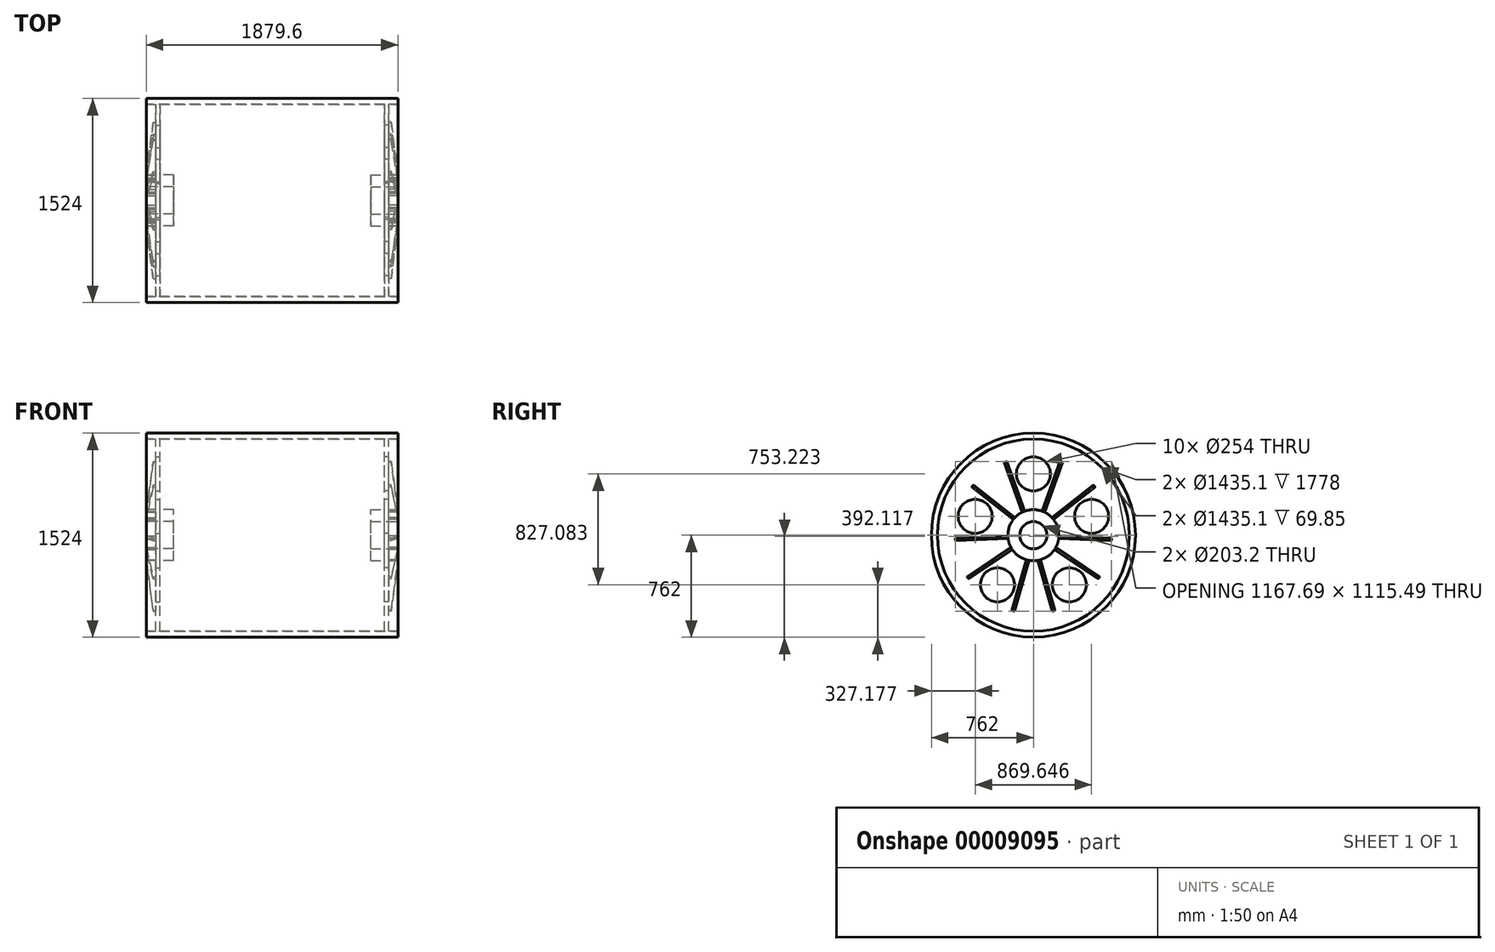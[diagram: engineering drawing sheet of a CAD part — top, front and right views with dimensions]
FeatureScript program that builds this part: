
annotation { "Feature Type Name" : "Feature", "Feature Type Description" : "" }
export const myFeature = defineFeature(function(context is Context, id is Id, definition is map)
    precondition{}
    {
        {
            var Q0;
            Q0=qCreatedBy(makeId("Right.planeOp"),FACE);
            var sketch = newSketch(context, id + "F0", { "sketchPlane" : qUnion([Q0])});
            skCircle(sketch, "E0", {"center": v(0, 0) * mm, "radius": 762 * mm});
            skCircle(sketch, "E1", {"center": v(0, 0) * mm, "radius": 717.55 * mm});
            skSolve(sketch);
        }
        {
            var Q0;
            Q0 = qSketchRegion(id + "F0", true);
            extrude(context, id + "F1", {"entities" : qUnion([Q0]), "endBound" : BoundingType.SYMMETRIC, "depth" : 1879.6 * mm});
        }
        {
            var Q0;
            Q0=makeQuery(id+"F1.opExtrude","CAP_FACE",FACE,{"disambiguationData":[OSD([sQuery(id+"F0.wireOp",EDGE,"E0"),sQuery(id+"F0.wireOp",EDGE,"E1")])],"isStart":false});
            cPlane(context, id + "F2", {"entities" : qUnion([Q0]), "cplaneType" : CPlaneType.OFFSET, "offset" : 101.6 * mm, "oppositeDirection" : true, "width" : 152.4 * mm, "height" : 152.4 * mm});
        }
        {
            var Q0;
            Q0=qCreatedBy(id+"F2.planeOp",FACE);
            var sketch = newSketch(context, id + "F3", { "sketchPlane" : qUnion([Q0])});
            skCircle(sketch, "E2.0", {"center": v(0, 0) * mm, "radius": 717.55 * mm});
            skCircle(sketch, "E3", {"center": v(0, 0) * mm, "radius": 190.5 * mm});
            skCircle(sketch, "E4", {"center": v(0, 0) * mm, "radius": 457.2 * mm, "construction": true});
            skLineSegment(sketch, "E5", {"start": v(0, 0) * mm, "end": v(0, 568.44) * mm, "construction": true});
            skCircle(sketch, "E6", {"center": v(0, 457.2) * mm, "radius": 127 * mm});
            skCircle(sketch, "E7.1.0", {"center": v(-434.82, 141.28) * mm, "radius": 127 * mm});
            skCircle(sketch, "E7.2.0", {"center": v(-268.74, -369.88) * mm, "radius": 127 * mm});
            skCircle(sketch, "E8.1.3.0", {"center": v(268.74, -369.88) * mm, "radius": 127 * mm});
            skCircle(sketch, "E8.1.4.0", {"center": v(434.82, 141.28) * mm, "radius": 127 * mm});
            skSolve(sketch);
        }
        {
            var Q0;
            Q0=makeQuery(id+"F3.imprint","IMPRINT",FACE,{"disambiguationData":[TD([[makeQuery(id+"F3.imprint","IMPRINT",EDGE,{"derivedFrom":sQuery(id+"F3.wireOp",EDGE,"E2.0")}),1.0]])]});
            extrude(context, id + "F4", {"entities" : qUnion([Q0]), "operationType" : NewBodyOperationType.ADD, "depth" : 31.75 * mm});
        }
        {
            var Q0;
            Q0=makeQuery(id+"F4.opExtrude","CAP_FACE",FACE,{"disambiguationData":[OSD([sQuery(id+"F3.wireOp",EDGE,"E2.0"),sQuery(id+"F3.wireOp",EDGE,"E3"),sQuery(id+"F3.wireOp",EDGE,"E6"),sQuery(id+"F3.wireOp",EDGE,"E7.1.0"),sQuery(id+"F3.wireOp",EDGE,"E7.2.0"),sQuery(id+"F3.wireOp",EDGE,"E8.1.3.0"),sQuery(id+"F3.wireOp",EDGE,"E8.1.4.0")])],"isStart":false});
            var sketch = newSketch(context, id + "F5", { "sketchPlane" : qUnion([Q0])});
            skLineSegment(sketch, "E9", {"start": v(-65.15, 179.01) * mm, "end": v(-199.8, 548.97) * mm});
            skLineSegment(sketch, "E10", {"start": v(0, 0) * mm, "end": v(0, 828.08) * mm, "construction": true});
            skLineSegment(sketch, "E11.0", {"start": v(-82.73, 171.6) * mm, "end": v(-217.6, 542.16) * mm});
            skCircle(sketch, "E12.0", {"center": v(0, 0) * mm, "radius": 190.5 * mm, "construction": true});
            skArc(sketch, "E13.0", {"start": v(-199.8, 548.97) * mm, "mid": v(-208.73, 545.64) * mm, "end": v(-217.6, 542.16) * mm});
            skLineSegment(sketch, "E14", {"start": v(-65.15, 179.01) * mm, "end": v(-82.73, 171.6) * mm});
            skSolve(sketch);
        }
        {
            var Q0;
            Q0 = qSketchRegion(id + "F5", true);
            var Q1;
            Q1=makeQuery(id+"F1.opExtrude","CAP_FACE",FACE,{"disambiguationData":[OSD([sQuery(id+"F0.wireOp",EDGE,"E0"),sQuery(id+"F0.wireOp",EDGE,"E1")])],"isStart":false});
            extrude(context, id + "F6", {"entities" : qUnion([Q0]), "endBound" : BoundingType.UP_TO_SURFACE, "endBoundEntityFace" : qUnion([Q1]), "depth" : 25.4 * mm});
        }
        {
            var Q0;
            Q0=makeQuery(id+"F6.opExtrude","SWEPT_FACE",FACE,{"disambiguationData":[OSD([sQuery(id+"F5.wireOp",EDGE,"E9")])]});
            var sketch = newSketch(context, id + "F7", { "sketchPlane" : qUnion([Q0])});
            skLineSegment(sketch, "E15.0", {"start": v(-889, -717.55) * mm, "end": v(-889, 717.55) * mm, "construction": true});
            skLineSegment(sketch, "E16.0", {"start": v(-939.8, 584.2) * mm, "end": v(-869.95, 584.2) * mm, "construction": true});
            skLineSegment(sketch, "E17.0", {"start": v(-939.8, 190.5) * mm, "end": v(-869.95, 190.5) * mm, "construction": true});
            skLineSegment(sketch, "E18", {"start": v(-889, 584.2) * mm, "end": v(-939.8, 190.5) * mm});
            skLineSegment(sketch, "E19", {"start": v(-889, 584.2) * mm, "end": v(-939.8, 584.2) * mm});
            skLineSegment(sketch, "E20", {"start": v(-939.8, 190.5) * mm, "end": v(-939.8, 584.2) * mm});
            skSolve(sketch);
        }
        {
            var Q0;
            Q0 = qSketchRegion(id + "F7", true);
            extrude(context, id + "F8", {"entities" : qUnion([Q0]), "operationType" : NewBodyOperationType.REMOVE, "oppositeDirection" : true, "depth" : 50.8 * mm});
        }
        {
            var Q0;
            Q0=makeQuery(id+"F6.opExtrude","SWEPT_BODY",BODY,{"disambiguationData":[OSD([sQuery(id+"F5.wireOp",EDGE,"E9"),sQuery(id+"F5.wireOp",EDGE,"E11.0"),sQuery(id+"F5.wireOp",EDGE,"E13.0"),sQuery(id+"F5.wireOp",EDGE,"E14")])]});
            var Q1;
            Q1=qCreatedBy(makeId("Front.planeOp"),FACE);
            mirror(context, id + "F9", {"entities" : qUnion([Q0]), "mirrorPlane" : qUnion([Q1])});
        }
        {
            var Q0;
            Q0=makeQuery(id+"F6.opExtrude","SWEPT_BODY",BODY,{"disambiguationData":[OSD([sQuery(id+"F5.wireOp",EDGE,"E9"),sQuery(id+"F5.wireOp",EDGE,"E11.0"),sQuery(id+"F5.wireOp",EDGE,"E13.0"),sQuery(id+"F5.wireOp",EDGE,"E14")])]});
            var Q1;
            Q1=makeQuery(id+"F9.opPattern","COPY",BODY,{"derivedFrom":makeQuery(id+"F6.opExtrude","SWEPT_BODY",BODY,{"disambiguationData":[OSD([sQuery(id+"F5.wireOp",EDGE,"E9"),sQuery(id+"F5.wireOp",EDGE,"E11.0"),sQuery(id+"F5.wireOp",EDGE,"E13.0"),sQuery(id+"F5.wireOp",EDGE,"E14")])]}),"instanceName":"1"});
            var Q2;
            Q2=makeQuery(id+"F4.opExtrude","CAP_EDGE",EDGE,{"disambiguationData":[OSD([sQuery(id+"F3.wireOp",EDGE,"E3")])],"isStart":true});
            circularPattern(context, id + "F10", {"entities" : qUnion([Q0, Q1]), "axis" : qUnion([Q2]), "angle" : 72 * degree, "instanceCount" : 5});
        }
        {
            var Q0;
            Q0=makeQuery(id+"F1.opExtrude","CAP_FACE",FACE,{"disambiguationData":[OSD([sQuery(id+"F0.wireOp",EDGE,"E0"),sQuery(id+"F0.wireOp",EDGE,"E1")])],"isStart":false});
            var sketch = newSketch(context, id + "F11", { "sketchPlane" : qUnion([Q0])});
            skCircle(sketch, "E21", {"center": v(0, 0) * mm, "radius": 190.5 * mm});
            skCircle(sketch, "E22", {"center": v(0, 0) * mm, "radius": 101.6 * mm});
            skSolve(sketch);
        }
        {
            var Q0;
            Q0 = qSketchRegion(id + "F11", true);
            extrude(context, id + "F12", {"entities" : qUnion([Q0]), "operationType" : NewBodyOperationType.ADD, "oppositeDirection" : true, "depth" : 203.2 * mm});
        }
        {
            var Q0;
            Q0=makeQuery(id+"F1.opExtrude","SWEPT_BODY",BODY,{"disambiguationData":[OSD([sQuery(id+"F0.wireOp",EDGE,"E0"),sQuery(id+"F0.wireOp",EDGE,"E1")])]});
            var Q1;
            Q1=makeQuery(id+"F4.opExtrude","SWEPT_FACE",FACE,{"disambiguationData":[OSD([sQuery(id+"F3.wireOp",EDGE,"E7.2.0")])]});
            var Q2;
            Q2=makeQuery(id+"F4.opExtrude","SWEPT_FACE",FACE,{"disambiguationData":[OSD([sQuery(id+"F3.wireOp",EDGE,"E6")])]});
            var Q3;
            Q3=makeQuery(id+"F4.opExtrude","SWEPT_FACE",FACE,{"disambiguationData":[OSD([sQuery(id+"F3.wireOp",EDGE,"E7.1.0")])]});
            var Q4;
            Q4=makeQuery(id+"F6.opExtrude","SWEPT_FACE",FACE,{"disambiguationData":[OSD([sQuery(id+"F5.wireOp",EDGE,"E11.0")])]});
            var Q5;
            {var subQ0=sQuery(id+"F11.wireOp",EDGE,"E21");var subQ5=makeQuery(id+"F8.boolean.opBoolean","COPY",FACE,{"derivedFrom":makeQuery(id+"F8.opExtrude","SWEPT_FACE",FACE,{"disambiguationData":[OSD([sQuery(id+"F7.wireOp",EDGE,"E18")])]})});Q5=makeQuery(id+"F12.boolean.opBoolean","SPLIT",FACE,{"disambiguationData":[TD([makeQuery(id+"F10.opPattern","COPY",FACE,{"derivedFrom":subQ5,"instanceName":"3"})])],"derivedFrom":makeQuery(id+"F12.opExtrude","SWEPT_FACE",FACE,{"disambiguationData":[OSD([subQ0])]})});}
            var Q6;
            Q6=makeQuery(id+"F4.opExtrude","CAP_FACE",FACE,{"disambiguationData":[OSD([sQuery(id+"F3.wireOp",EDGE,"E2.0"),sQuery(id+"F3.wireOp",EDGE,"E3"),sQuery(id+"F3.wireOp",EDGE,"E6"),sQuery(id+"F3.wireOp",EDGE,"E7.1.0"),sQuery(id+"F3.wireOp",EDGE,"E7.2.0"),sQuery(id+"F3.wireOp",EDGE,"E8.1.3.0"),sQuery(id+"F3.wireOp",EDGE,"E8.1.4.0")])],"isStart":true});
            var Q7;
            Q7=makeQuery(id+"F4.opExtrude","SWEPT_FACE",FACE,{"disambiguationData":[OSD([sQuery(id+"F3.wireOp",EDGE,"E8.1.3.0")])]});
            var Q8;
            Q8=makeQuery(id+"F4.opExtrude","SWEPT_FACE",FACE,{"disambiguationData":[OSD([sQuery(id+"F3.wireOp",EDGE,"E8.1.4.0")])]});
            var Q9;
            {var subQ3=makeQuery(id+"F6.opExtrude","SWEPT_FACE",FACE,{"disambiguationData":[OSD([sQuery(id+"F5.wireOp",EDGE,"E11.0")])]});var subQ4=sQuery(id+"F11.wireOp",EDGE,"E21");Q9=makeQuery(id+"F12.boolean.opBoolean","SPLIT",FACE,{"disambiguationData":[TD([makeQuery(id+"F10.opPattern","COPY",FACE,{"derivedFrom":subQ3,"instanceName":"2"})])],"derivedFrom":makeQuery(id+"F12.opExtrude","SWEPT_FACE",FACE,{"disambiguationData":[OSD([subQ4])]})});}
            var Q10;
            Q10=makeQuery(id+"F9.opPattern","COPY",FACE,{"derivedFrom":makeQuery(id+"F6.opExtrude","SWEPT_FACE",FACE,{"disambiguationData":[OSD([sQuery(id+"F5.wireOp",EDGE,"E13.0")])]}),"instanceName":"1"});
            var Q11;
            Q11=makeQuery(id+"F6.opExtrude","SWEPT_FACE",FACE,{"disambiguationData":[OSD([sQuery(id+"F5.wireOp",EDGE,"E13.0")])]});
            var Q12;
            Q12=makeQuery(id+"F8.boolean.opBoolean","COPY",FACE,{"derivedFrom":makeQuery(id+"F8.opExtrude","SWEPT_FACE",FACE,{"disambiguationData":[OSD([sQuery(id+"F7.wireOp",EDGE,"E18")])]})});
            var Q13;
            Q13=makeQuery(id+"F6.opExtrude","SWEPT_FACE",FACE,{"disambiguationData":[OSD([sQuery(id+"F5.wireOp",EDGE,"E9")])]});
            var Q14;
            {var subQ0=sQuery(id+"F0.wireOp",EDGE,"E1");Q14=makeQuery(id+"F4.boolean.opBoolean","SPLIT",FACE,{"disambiguationData":[TD([makeQuery(id+"F1.opExtrude","CAP_FACE",FACE,{"disambiguationData":[OSD([sQuery(id+"F0.wireOp",EDGE,"E0"),subQ0])],"isStart":false})])],"derivedFrom":makeQuery(id+"F1.opExtrude","SWEPT_FACE",FACE,{"disambiguationData":[OSD([subQ0])]})});}
            var Q15;
            Q15=makeQuery(id+"F1.opExtrude","CAP_FACE",FACE,{"disambiguationData":[OSD([sQuery(id+"F0.wireOp",EDGE,"E0"),sQuery(id+"F0.wireOp",EDGE,"E1")])],"isStart":false});
            var Q16;
            Q16=makeQuery(id+"F9.opPattern","COPY",FACE,{"derivedFrom":makeQuery(id+"F6.opExtrude","SWEPT_FACE",FACE,{"disambiguationData":[OSD([sQuery(id+"F5.wireOp",EDGE,"E9")])]}),"instanceName":"1"});
            var Q17;
            Q17=makeQuery(id+"F9.opPattern","COPY",FACE,{"derivedFrom":makeQuery(id+"F8.boolean.opBoolean","COPY",FACE,{"derivedFrom":makeQuery(id+"F8.opExtrude","SWEPT_FACE",FACE,{"disambiguationData":[OSD([sQuery(id+"F7.wireOp",EDGE,"E18")])]})}),"instanceName":"1"});
            var Q18;
            Q18=makeQuery(id+"F9.opPattern","COPY",FACE,{"derivedFrom":makeQuery(id+"F6.opExtrude","SWEPT_FACE",FACE,{"disambiguationData":[OSD([sQuery(id+"F5.wireOp",EDGE,"E11.0")])]}),"instanceName":"1"});
            var Q19;
            Q19=makeQuery(id+"F10.opPattern","COPY",FACE,{"derivedFrom":makeQuery(id+"F9.opPattern","COPY",FACE,{"derivedFrom":makeQuery(id+"F8.boolean.opBoolean","COPY",FACE,{"derivedFrom":makeQuery(id+"F8.opExtrude","SWEPT_FACE",FACE,{"disambiguationData":[OSD([sQuery(id+"F7.wireOp",EDGE,"E18")])]})}),"instanceName":"1"}),"instanceName":"4"});
            var Q20;
            Q20=makeQuery(id+"F10.opPattern","COPY",FACE,{"derivedFrom":makeQuery(id+"F9.opPattern","COPY",FACE,{"derivedFrom":makeQuery(id+"F6.opExtrude","SWEPT_FACE",FACE,{"disambiguationData":[OSD([sQuery(id+"F5.wireOp",EDGE,"E9")])]}),"instanceName":"1"}),"instanceName":"3"});
            var Q21;
            Q21=makeQuery(id+"F10.opPattern","COPY",FACE,{"derivedFrom":makeQuery(id+"F9.opPattern","COPY",FACE,{"derivedFrom":makeQuery(id+"F6.opExtrude","SWEPT_FACE",FACE,{"disambiguationData":[OSD([sQuery(id+"F5.wireOp",EDGE,"E11.0")])]}),"instanceName":"1"}),"instanceName":"4"});
            var Q22;
            Q22=makeQuery(id+"F10.opPattern","COPY",FACE,{"derivedFrom":makeQuery(id+"F6.opExtrude","SWEPT_FACE",FACE,{"disambiguationData":[OSD([sQuery(id+"F5.wireOp",EDGE,"E9")])]}),"instanceName":"4"});
            var Q23;
            Q23=makeQuery(id+"F10.opPattern","COPY",FACE,{"derivedFrom":makeQuery(id+"F8.boolean.opBoolean","COPY",FACE,{"derivedFrom":makeQuery(id+"F8.opExtrude","SWEPT_FACE",FACE,{"disambiguationData":[OSD([sQuery(id+"F7.wireOp",EDGE,"E18")])]})}),"instanceName":"1"});
            var Q24;
            {var subQ3=makeQuery(id+"F6.opExtrude","SWEPT_FACE",FACE,{"disambiguationData":[OSD([sQuery(id+"F5.wireOp",EDGE,"E11.0")])]});var subQ4=sQuery(id+"F11.wireOp",EDGE,"E21");Q24=makeQuery(id+"F12.boolean.opBoolean","SPLIT",FACE,{"disambiguationData":[TD([subQ3])],"derivedFrom":makeQuery(id+"F12.opExtrude","SWEPT_FACE",FACE,{"disambiguationData":[OSD([subQ4])]})});}
            var Q25;
            Q25=makeQuery(id+"F10.opPattern","COPY",FACE,{"derivedFrom":makeQuery(id+"F9.opPattern","COPY",FACE,{"derivedFrom":makeQuery(id+"F6.opExtrude","SWEPT_FACE",FACE,{"disambiguationData":[OSD([sQuery(id+"F5.wireOp",EDGE,"E13.0")])]}),"instanceName":"1"}),"instanceName":"1"});
            var Q26;
            Q26=makeQuery(id+"F12.opExtrude","CAP_FACE",FACE,{"disambiguationData":[OSD([sQuery(id+"F11.wireOp",EDGE,"E21"),sQuery(id+"F11.wireOp",EDGE,"E22")])],"isStart":false});
            var Q27;
            Q27=makeQuery(id+"F10.opPattern","COPY",FACE,{"derivedFrom":makeQuery(id+"F9.opPattern","COPY",FACE,{"derivedFrom":makeQuery(id+"F6.opExtrude","SWEPT_FACE",FACE,{"disambiguationData":[OSD([sQuery(id+"F5.wireOp",EDGE,"E9")])]}),"instanceName":"1"}),"instanceName":"4"});
            var Q28;
            Q28=makeQuery(id+"F10.opPattern","COPY",FACE,{"derivedFrom":makeQuery(id+"F6.opExtrude","SWEPT_FACE",FACE,{"disambiguationData":[OSD([sQuery(id+"F5.wireOp",EDGE,"E13.0")])]}),"instanceName":"3"});
            var Q29;
            Q29=makeQuery(id+"F4.opExtrude","CAP_FACE",FACE,{"disambiguationData":[OSD([sQuery(id+"F3.wireOp",EDGE,"E2.0"),sQuery(id+"F3.wireOp",EDGE,"E3"),sQuery(id+"F3.wireOp",EDGE,"E6"),sQuery(id+"F3.wireOp",EDGE,"E7.1.0"),sQuery(id+"F3.wireOp",EDGE,"E7.2.0"),sQuery(id+"F3.wireOp",EDGE,"E8.1.3.0"),sQuery(id+"F3.wireOp",EDGE,"E8.1.4.0")])],"isStart":false});
            var Q30;
            Q30=makeQuery(id+"F10.opPattern","COPY",FACE,{"derivedFrom":makeQuery(id+"F6.opExtrude","SWEPT_FACE",FACE,{"disambiguationData":[OSD([sQuery(id+"F5.wireOp",EDGE,"E11.0")])]}),"instanceName":"1"});
            var Q31;
            Q31=makeQuery(id+"F10.opPattern","COPY",FACE,{"derivedFrom":makeQuery(id+"F9.opPattern","COPY",FACE,{"derivedFrom":makeQuery(id+"F6.opExtrude","SWEPT_FACE",FACE,{"disambiguationData":[OSD([sQuery(id+"F5.wireOp",EDGE,"E11.0")])]}),"instanceName":"1"}),"instanceName":"2"});
            var Q32;
            Q32=makeQuery(id+"F10.opPattern","COPY",FACE,{"derivedFrom":makeQuery(id+"F6.opExtrude","SWEPT_FACE",FACE,{"disambiguationData":[OSD([sQuery(id+"F5.wireOp",EDGE,"E9")])]}),"instanceName":"1"});
            var Q33;
            {var subQ0=makeQuery(id+"F6.opExtrude","SWEPT_FACE",FACE,{"disambiguationData":[OSD([sQuery(id+"F5.wireOp",EDGE,"E9")])]});var subQ5=sQuery(id+"F11.wireOp",EDGE,"E21");Q33=makeQuery(id+"F12.boolean.opBoolean","SPLIT",FACE,{"disambiguationData":[TD([subQ0])],"derivedFrom":makeQuery(id+"F12.opExtrude","SWEPT_FACE",FACE,{"disambiguationData":[OSD([subQ5])]})});}
            var Q34;
            {var subQ0=sQuery(id+"F11.wireOp",EDGE,"E21");var subQ6=makeQuery(id+"F8.boolean.opBoolean","COPY",FACE,{"derivedFrom":makeQuery(id+"F8.opExtrude","SWEPT_FACE",FACE,{"disambiguationData":[OSD([sQuery(id+"F7.wireOp",EDGE,"E18")])]})});Q34=makeQuery(id+"F12.boolean.opBoolean","SPLIT",FACE,{"disambiguationData":[TD([makeQuery(id+"F10.opPattern","COPY",FACE,{"derivedFrom":subQ6,"instanceName":"2"})])],"derivedFrom":makeQuery(id+"F12.opExtrude","SWEPT_FACE",FACE,{"disambiguationData":[OSD([subQ0])]})});}
            var Q35;
            Q35=makeQuery(id+"F10.opPattern","COPY",FACE,{"derivedFrom":makeQuery(id+"F6.opExtrude","SWEPT_FACE",FACE,{"disambiguationData":[OSD([sQuery(id+"F5.wireOp",EDGE,"E11.0")])]}),"instanceName":"2"});
            var Q36;
            Q36=makeQuery(id+"F10.opPattern","COPY",FACE,{"derivedFrom":makeQuery(id+"F6.opExtrude","SWEPT_FACE",FACE,{"disambiguationData":[OSD([sQuery(id+"F5.wireOp",EDGE,"E11.0")])]}),"instanceName":"4"});
            var Q37;
            Q37=makeQuery(id+"F10.opPattern","COPY",FACE,{"derivedFrom":makeQuery(id+"F6.opExtrude","SWEPT_FACE",FACE,{"disambiguationData":[OSD([sQuery(id+"F5.wireOp",EDGE,"E9")])]}),"instanceName":"3"});
            var Q38;
            Q38=makeQuery(id+"F10.opPattern","COPY",FACE,{"derivedFrom":makeQuery(id+"F9.opPattern","COPY",FACE,{"derivedFrom":makeQuery(id+"F6.opExtrude","SWEPT_FACE",FACE,{"disambiguationData":[OSD([sQuery(id+"F5.wireOp",EDGE,"E11.0")])]}),"instanceName":"1"}),"instanceName":"1"});
            var Q39;
            Q39=makeQuery(id+"F10.opPattern","COPY",FACE,{"derivedFrom":makeQuery(id+"F9.opPattern","COPY",FACE,{"derivedFrom":makeQuery(id+"F8.boolean.opBoolean","COPY",FACE,{"derivedFrom":makeQuery(id+"F8.opExtrude","SWEPT_FACE",FACE,{"disambiguationData":[OSD([sQuery(id+"F7.wireOp",EDGE,"E18")])]})}),"instanceName":"1"}),"instanceName":"1"});
            var Q40;
            {var subQ0=makeQuery(id+"F6.opExtrude","CAP_FACE",FACE,{"disambiguationData":[OSD([sQuery(id+"F0.wireOp",EDGE,"E0"),sQuery(id+"F0.wireOp",EDGE,"E1")])],"isStart":false});var subQ1=makeQuery(id+"F9.opPattern","COPY",FACE,{"derivedFrom":subQ0,"instanceName":"1"});Q40=makeQuery(id+"F12.boolean.opBoolean","MERGE",FACE,{"derivedFrom":[subQ0,subQ1,makeQuery(id+"F10.opPattern","COPY",FACE,{"derivedFrom":subQ0,"instanceName":"1"}),makeQuery(id+"F10.opPattern","COPY",FACE,{"derivedFrom":subQ1,"instanceName":"1"}),makeQuery(id+"F10.opPattern","COPY",FACE,{"derivedFrom":subQ0,"instanceName":"2"}),makeQuery(id+"F10.opPattern","COPY",FACE,{"derivedFrom":subQ1,"instanceName":"2"}),makeQuery(id+"F10.opPattern","COPY",FACE,{"derivedFrom":subQ0,"instanceName":"3"}),makeQuery(id+"F10.opPattern","COPY",FACE,{"derivedFrom":subQ1,"instanceName":"3"}),makeQuery(id+"F10.opPattern","COPY",FACE,{"derivedFrom":subQ0,"instanceName":"4"}),makeQuery(id+"F10.opPattern","COPY",FACE,{"derivedFrom":subQ1,"instanceName":"4"}),makeQuery(id+"F12.opExtrude","CAP_FACE",FACE,{"disambiguationData":[OSD([sQuery(id+"F11.wireOp",EDGE,"E21"),sQuery(id+"F11.wireOp",EDGE,"E22")])],"isStart":true})]});}
            var Q41;
            Q41=makeQuery(id+"F10.opPattern","COPY",FACE,{"derivedFrom":makeQuery(id+"F9.opPattern","COPY",FACE,{"derivedFrom":makeQuery(id+"F6.opExtrude","SWEPT_FACE",FACE,{"disambiguationData":[OSD([sQuery(id+"F5.wireOp",EDGE,"E9")])]}),"instanceName":"1"}),"instanceName":"1"});
            var Q42;
            Q42=makeQuery(id+"F10.opPattern","COPY",FACE,{"derivedFrom":makeQuery(id+"F9.opPattern","COPY",FACE,{"derivedFrom":makeQuery(id+"F6.opExtrude","SWEPT_FACE",FACE,{"disambiguationData":[OSD([sQuery(id+"F5.wireOp",EDGE,"E9")])]}),"instanceName":"1"}),"instanceName":"2"});
            var Q43;
            {var subQ2=makeQuery(id+"F6.opExtrude","SWEPT_FACE",FACE,{"disambiguationData":[OSD([sQuery(id+"F5.wireOp",EDGE,"E11.0")])]});var subQ4=sQuery(id+"F11.wireOp",EDGE,"E21");Q43=makeQuery(id+"F12.boolean.opBoolean","SPLIT",FACE,{"disambiguationData":[TD([makeQuery(id+"F10.opPattern","COPY",FACE,{"derivedFrom":subQ2,"instanceName":"1"})])],"derivedFrom":makeQuery(id+"F12.opExtrude","SWEPT_FACE",FACE,{"disambiguationData":[OSD([subQ4])]})});}
            var Q44;
            {var subQ0=sQuery(id+"F11.wireOp",EDGE,"E21");var subQ6=makeQuery(id+"F8.boolean.opBoolean","COPY",FACE,{"derivedFrom":makeQuery(id+"F8.opExtrude","SWEPT_FACE",FACE,{"disambiguationData":[OSD([sQuery(id+"F7.wireOp",EDGE,"E18")])]})});Q44=makeQuery(id+"F12.boolean.opBoolean","SPLIT",FACE,{"disambiguationData":[TD([makeQuery(id+"F10.opPattern","COPY",FACE,{"derivedFrom":subQ6,"instanceName":"4"})])],"derivedFrom":makeQuery(id+"F12.opExtrude","SWEPT_FACE",FACE,{"disambiguationData":[OSD([subQ0])]})});}
            var Q45;
            Q45=makeQuery(id+"F10.opPattern","COPY",FACE,{"derivedFrom":makeQuery(id+"F9.opPattern","COPY",FACE,{"derivedFrom":makeQuery(id+"F6.opExtrude","SWEPT_FACE",FACE,{"disambiguationData":[OSD([sQuery(id+"F5.wireOp",EDGE,"E13.0")])]}),"instanceName":"1"}),"instanceName":"2"});
            var Q46;
            {var subQ0=makeQuery(id+"F6.opExtrude","SWEPT_FACE",FACE,{"disambiguationData":[OSD([sQuery(id+"F5.wireOp",EDGE,"E11.0")])]});var subQ4=sQuery(id+"F11.wireOp",EDGE,"E21");Q46=makeQuery(id+"F12.boolean.opBoolean","SPLIT",FACE,{"disambiguationData":[TD([makeQuery(id+"F10.opPattern","COPY",FACE,{"derivedFrom":subQ0,"instanceName":"3"})])],"derivedFrom":makeQuery(id+"F12.opExtrude","SWEPT_FACE",FACE,{"disambiguationData":[OSD([subQ4])]})});}
            var Q47;
            Q47=makeQuery(id+"F10.opPattern","COPY",FACE,{"derivedFrom":makeQuery(id+"F6.opExtrude","SWEPT_FACE",FACE,{"disambiguationData":[OSD([sQuery(id+"F5.wireOp",EDGE,"E9")])]}),"instanceName":"2"});
            var Q48;
            Q48=makeQuery(id+"F10.opPattern","COPY",FACE,{"derivedFrom":makeQuery(id+"F6.opExtrude","SWEPT_FACE",FACE,{"disambiguationData":[OSD([sQuery(id+"F5.wireOp",EDGE,"E11.0")])]}),"instanceName":"3"});
            var Q49;
            Q49=makeQuery(id+"F10.opPattern","COPY",FACE,{"derivedFrom":makeQuery(id+"F9.opPattern","COPY",FACE,{"derivedFrom":makeQuery(id+"F6.opExtrude","SWEPT_FACE",FACE,{"disambiguationData":[OSD([sQuery(id+"F5.wireOp",EDGE,"E13.0")])]}),"instanceName":"1"}),"instanceName":"4"});
            var Q50;
            Q50=makeQuery(id+"F10.opPattern","COPY",FACE,{"derivedFrom":makeQuery(id+"F9.opPattern","COPY",FACE,{"derivedFrom":makeQuery(id+"F8.boolean.opBoolean","COPY",FACE,{"derivedFrom":makeQuery(id+"F8.opExtrude","SWEPT_FACE",FACE,{"disambiguationData":[OSD([sQuery(id+"F7.wireOp",EDGE,"E18")])]})}),"instanceName":"1"}),"instanceName":"2"});
            var Q51;
            {var subQ3=sQuery(id+"F11.wireOp",EDGE,"E21");var subQ4=makeQuery(id+"F6.opExtrude","SWEPT_FACE",FACE,{"disambiguationData":[OSD([sQuery(id+"F5.wireOp",EDGE,"E11.0")])]});Q51=makeQuery(id+"F12.boolean.opBoolean","SPLIT",FACE,{"disambiguationData":[TD([makeQuery(id+"F9.opPattern","COPY",FACE,{"derivedFrom":subQ4,"instanceName":"1"})])],"derivedFrom":makeQuery(id+"F12.opExtrude","SWEPT_FACE",FACE,{"disambiguationData":[OSD([subQ3])]})});}
            var Q52;
            Q52=makeQuery(id+"F10.opPattern","COPY",FACE,{"derivedFrom":makeQuery(id+"F8.boolean.opBoolean","COPY",FACE,{"derivedFrom":makeQuery(id+"F8.opExtrude","SWEPT_FACE",FACE,{"disambiguationData":[OSD([sQuery(id+"F7.wireOp",EDGE,"E18")])]})}),"instanceName":"3"});
            var Q53;
            Q53=makeQuery(id+"F10.opPattern","COPY",FACE,{"derivedFrom":makeQuery(id+"F8.boolean.opBoolean","COPY",FACE,{"derivedFrom":makeQuery(id+"F8.opExtrude","SWEPT_FACE",FACE,{"disambiguationData":[OSD([sQuery(id+"F7.wireOp",EDGE,"E18")])]})}),"instanceName":"4"});
            var Q54;
            Q54=makeQuery(id+"F10.opPattern","COPY",FACE,{"derivedFrom":makeQuery(id+"F6.opExtrude","SWEPT_FACE",FACE,{"disambiguationData":[OSD([sQuery(id+"F5.wireOp",EDGE,"E13.0")])]}),"instanceName":"4"});
            var Q55;
            Q55=makeQuery(id+"F10.opPattern","COPY",FACE,{"derivedFrom":makeQuery(id+"F8.boolean.opBoolean","COPY",FACE,{"derivedFrom":makeQuery(id+"F8.opExtrude","SWEPT_FACE",FACE,{"disambiguationData":[OSD([sQuery(id+"F7.wireOp",EDGE,"E18")])]})}),"instanceName":"2"});
            var Q56;
            Q56=makeQuery(id+"F10.opPattern","COPY",FACE,{"derivedFrom":makeQuery(id+"F9.opPattern","COPY",FACE,{"derivedFrom":makeQuery(id+"F8.boolean.opBoolean","COPY",FACE,{"derivedFrom":makeQuery(id+"F8.opExtrude","SWEPT_FACE",FACE,{"disambiguationData":[OSD([sQuery(id+"F7.wireOp",EDGE,"E18")])]})}),"instanceName":"1"}),"instanceName":"3"});
            var Q57;
            Q57=makeQuery(id+"F12.opExtrude","SWEPT_FACE",FACE,{"disambiguationData":[OSD([sQuery(id+"F11.wireOp",EDGE,"E22")])]});
            var Q58;
            Q58=makeQuery(id+"F10.opPattern","COPY",FACE,{"derivedFrom":makeQuery(id+"F9.opPattern","COPY",FACE,{"derivedFrom":makeQuery(id+"F6.opExtrude","SWEPT_FACE",FACE,{"disambiguationData":[OSD([sQuery(id+"F5.wireOp",EDGE,"E13.0")])]}),"instanceName":"1"}),"instanceName":"3"});
            var Q59;
            Q59=makeQuery(id+"F10.opPattern","COPY",FACE,{"derivedFrom":makeQuery(id+"F6.opExtrude","SWEPT_FACE",FACE,{"disambiguationData":[OSD([sQuery(id+"F5.wireOp",EDGE,"E13.0")])]}),"instanceName":"2"});
            var Q60;
            {var subQ0=sQuery(id+"F11.wireOp",EDGE,"E21");var subQ6=makeQuery(id+"F8.boolean.opBoolean","COPY",FACE,{"derivedFrom":makeQuery(id+"F8.opExtrude","SWEPT_FACE",FACE,{"disambiguationData":[OSD([sQuery(id+"F7.wireOp",EDGE,"E18")])]})});Q60=makeQuery(id+"F12.boolean.opBoolean","SPLIT",FACE,{"disambiguationData":[TD([makeQuery(id+"F10.opPattern","COPY",FACE,{"derivedFrom":subQ6,"instanceName":"1"})])],"derivedFrom":makeQuery(id+"F12.opExtrude","SWEPT_FACE",FACE,{"disambiguationData":[OSD([subQ0])]})});}
            var Q61;
            Q61=makeQuery(id+"F10.opPattern","COPY",FACE,{"derivedFrom":makeQuery(id+"F6.opExtrude","SWEPT_FACE",FACE,{"disambiguationData":[OSD([sQuery(id+"F5.wireOp",EDGE,"E13.0")])]}),"instanceName":"1"});
            var Q62;
            {var subQ0=sQuery(id+"F11.wireOp",EDGE,"E21");Q62=makeQuery(id+"F12.boolean.opBoolean","SPLIT",FACE,{"disambiguationData":[TD([makeQuery(id+"F12.opExtrude","CAP_FACE",FACE,{"disambiguationData":[OSD([subQ0,sQuery(id+"F11.wireOp",EDGE,"E22")])],"isStart":false})])],"derivedFrom":makeQuery(id+"F12.opExtrude","SWEPT_FACE",FACE,{"disambiguationData":[OSD([subQ0])]})});}
            var Q63;
            Q63=makeQuery(id+"F10.opPattern","COPY",FACE,{"derivedFrom":makeQuery(id+"F9.opPattern","COPY",FACE,{"derivedFrom":makeQuery(id+"F6.opExtrude","SWEPT_FACE",FACE,{"disambiguationData":[OSD([sQuery(id+"F5.wireOp",EDGE,"E11.0")])]}),"instanceName":"1"}),"instanceName":"3"});
            var Q64;
            Q64=qCreatedBy(makeId("Right.planeOp"),FACE);
            mirror(context, id + "F13", {"entities" : qUnion([Q0]), "faces" : qUnion([Q1, Q2, Q3, Q4, Q5, Q6, Q7, Q8, Q9, Q10, Q11, Q12, Q13, Q14, Q15, Q16, Q17, Q18, Q19, Q20, Q21, Q22, Q23, Q24, Q25, Q26, Q27, Q28, Q29, Q30, Q31, Q32, Q33, Q34, Q35, Q36, Q37, Q38, Q39, Q40, Q41, Q42, Q43, Q44, Q45, Q46, Q47, Q48, Q49, Q50, Q51, Q52, Q53, Q54, Q55, Q56, Q57, Q58, Q59, Q60, Q61, Q62, Q63]), "mirrorPlane" : qUnion([Q64])});
        }
    });
